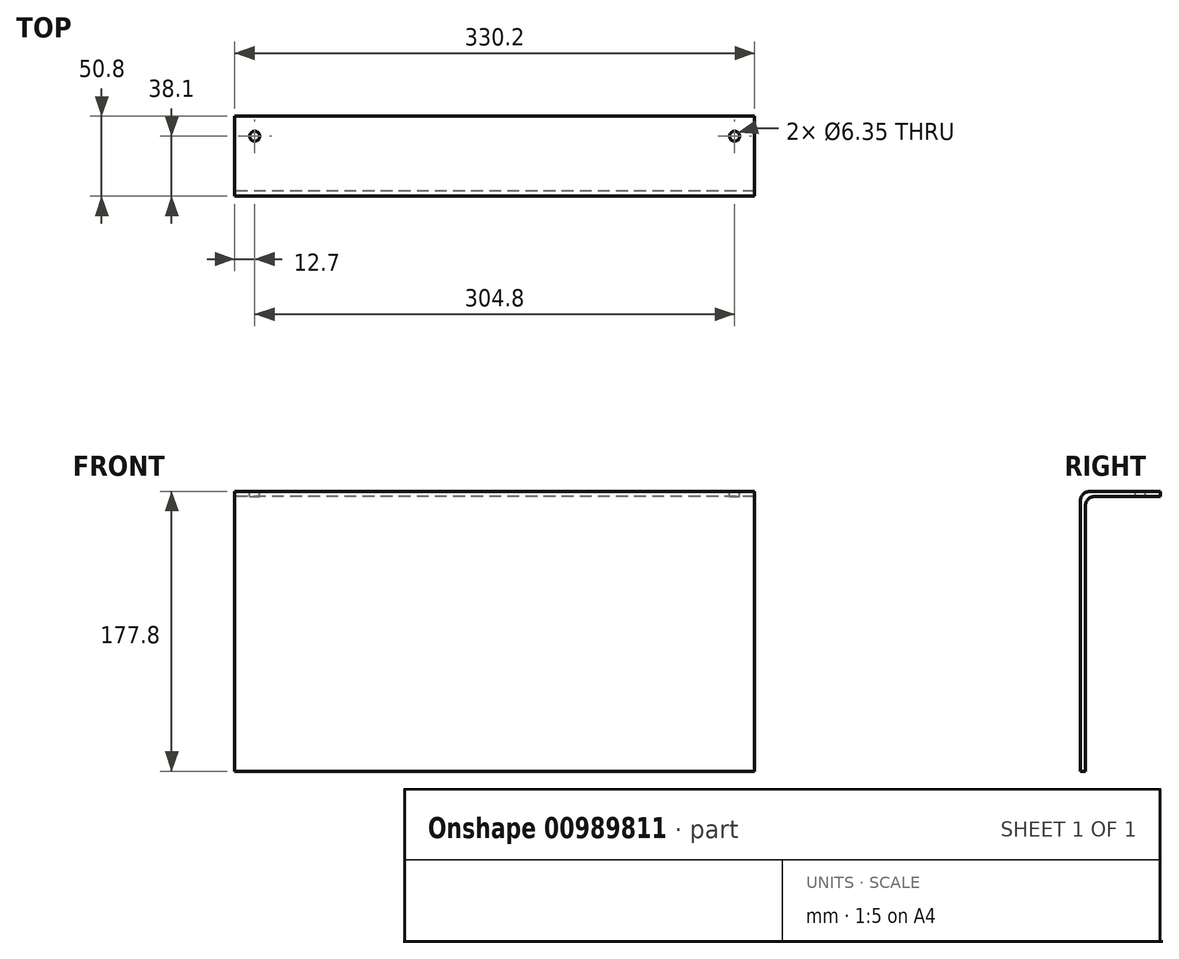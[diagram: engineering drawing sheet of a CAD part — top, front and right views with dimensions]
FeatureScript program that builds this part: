
annotation { "Feature Type Name" : "Feature", "Feature Type Description" : "" }
export const myFeature = defineFeature(function(context is Context, id is Id, definition is map)
    precondition{}
    {
        {
            var Q0;
            Q0=qCreatedBy(makeId("Right.planeOp"),FACE);
            var sketch = newSketch(context, id + "F0", { "sketchPlane" : qUnion([Q0])});
            skLineSegment(sketch, "E0", {"start": v(0, 0) * mm, "end": v(0, 171.45) * mm});
            skLineSegment(sketch, "E1", {"start": v(6.35, 177.8) * mm, "end": v(50.8, 177.8) * mm});
            skLineSegment(sketch, "E2", {"start": v(50.8, 177.8) * mm, "end": v(50.8, 174.62) * mm});
            skLineSegment(sketch, "E3", {"start": v(50.8, 174.62) * mm, "end": v(9.52, 174.62) * mm});
            skLineSegment(sketch, "E4", {"start": v(3.17, 168.28) * mm, "end": v(3.17, 0) * mm});
            skLineSegment(sketch, "E5", {"start": v(3.17, 0) * mm, "end": v(0, 0) * mm});
            skPoint(sketch, "E6.visualSharp", {"position": v(3.17, 174.62) * mm});
            skArc(sketch, "E6.filletArc", {"start": v(9.52, 174.62) * mm, "mid": v(5.03, 172.77) * mm, "end": v(3.17, 168.28) * mm});
            skPoint(sketch, "E7.visualSharp", {"position": v(0, 177.8) * mm});
            skArc(sketch, "E7.filletArc", {"start": v(6.35, 177.8) * mm, "mid": v(1.86, 175.94) * mm, "end": v(0, 171.45) * mm});
            skSolve(sketch);
        }
        {
            var Q0;
            Q0=makeQuery(id+"F0.imprint","IMPRINT",FACE,{"disambiguationData":[TD([[makeQuery(id+"F0.imprint","IMPRINT",EDGE,{"derivedFrom":sQuery(id+"F0.wireOp",EDGE,"E0")}),-1.0]])]});
            extrude(context, id + "F1", {"entities" : qUnion([Q0]), "depth" : 330.2 * mm, "offsetDistance" : 25.4 * mm});
        }
        {
            var Q0;
            Q0=makeQuery(id+"F1.opExtrude","SWEPT_FACE",FACE,{"disambiguationData":[OSD([sQuery(id+"F0.wireOp",EDGE,"E1")])]});
            var sketch = newSketch(context, id + "F2", { "sketchPlane" : qUnion([Q0])});
            skCircle(sketch, "E8", {"center": v(12.7, 38.1) * mm, "radius": 3.18 * mm});
            skCircle(sketch, "E9", {"center": v(317.5, 38.1) * mm, "radius": 3.18 * mm});
            skSolve(sketch);
        }
        {
            var Q0;
            Q0 = qSketchRegion(id + "F2", true);
            extrude(context, id + "F3", {"entities" : qUnion([Q0]), "operationType" : NewBodyOperationType.REMOVE, "endBound" : BoundingType.THROUGH_ALL, "oppositeDirection" : true, "depth" : 25.4 * mm, "offsetDistance" : 25.4 * mm});
        }
    });
